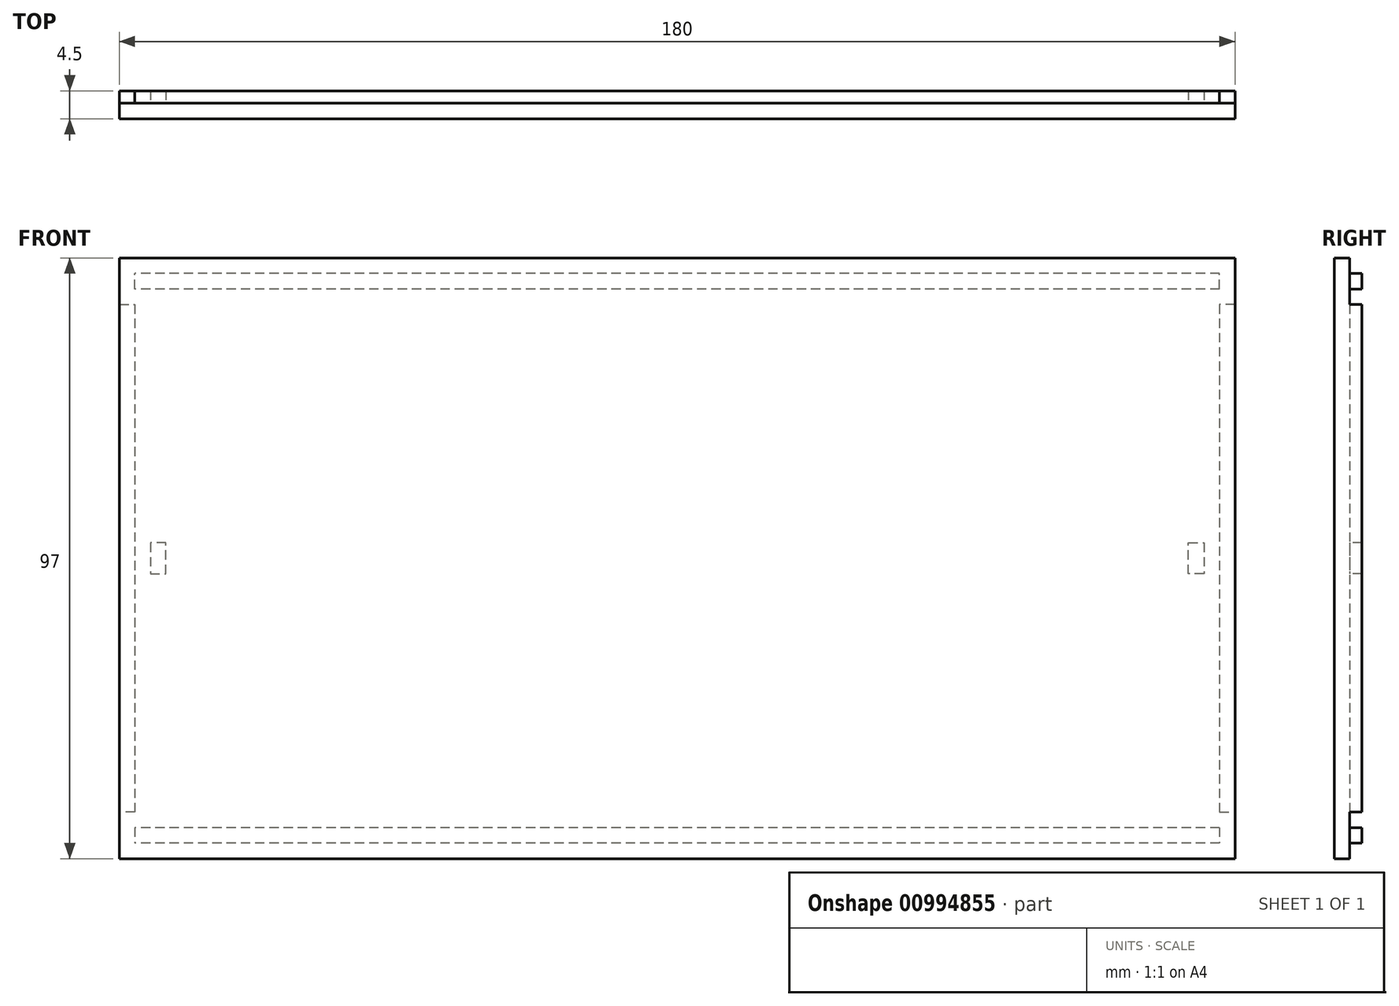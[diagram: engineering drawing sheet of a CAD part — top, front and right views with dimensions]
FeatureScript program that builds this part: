
annotation { "Feature Type Name" : "Feature", "Feature Type Description" : "" }
export const myFeature = defineFeature(function(context is Context, id is Id, definition is map)
    precondition{}
    {
        {
            var Q0;
            Q0=qCreatedBy(makeId("Front.planeOp"),FACE);
            var sketch = newSketch(context, id + "F0", { "sketchPlane" : qUnion([Q0])});
            skLineSegment(sketch, "E0.bottom", {"start": v(-85.95, 51.9) * mm, "end": v(94.05, 51.9) * mm});
            skLineSegment(sketch, "E0.top", {"start": v(-85.95, -45.1) * mm, "end": v(94.05, -45.1) * mm});
            skLineSegment(sketch, "E0.left", {"start": v(-85.95, 51.9) * mm, "end": v(-85.95, -45.1) * mm});
            skLineSegment(sketch, "E0.right", {"start": v(94.05, 51.9) * mm, "end": v(94.05, -45.1) * mm});
            skSolve(sketch);
        }
        {
            var Q0;
            Q0=makeQuery(id+"F0.imprint","IMPRINT",FACE,{"disambiguationData":[TD([[makeQuery(id+"F0.imprint","IMPRINT",EDGE,{"derivedFrom":sQuery(id+"F0.wireOp",EDGE,"E0.bottom")}),-1.0]])]});
            extrude(context, id + "F1", {"entities" : qUnion([Q0]), "depth" : 2.5 * mm, "offsetDistance" : 25 * mm});
        }
        {
            var Q0;
            Q0=makeQuery(id+"F1.opExtrude","CAP_FACE",FACE,{"disambiguationData":[OSD([sQuery(id+"F0.wireOp",EDGE,"E0.bottom"),sQuery(id+"F0.wireOp",EDGE,"E0.top"),sQuery(id+"F0.wireOp",EDGE,"E0.left"),sQuery(id+"F0.wireOp",EDGE,"E0.right")])],"isStart":true});
            var sketch = newSketch(context, id + "F2", { "sketchPlane" : qUnion([Q0])});
            skLineSegment(sketch, "E1.bottom", {"start": v(-91.55, -40.1) * mm, "end": v(83.45, -40.1) * mm});
            skLineSegment(sketch, "E1.top", {"start": v(-91.55, -42.6) * mm, "end": v(83.45, -42.6) * mm});
            skLineSegment(sketch, "E1.left", {"start": v(-91.55, -40.1) * mm, "end": v(-91.55, -42.6) * mm});
            skLineSegment(sketch, "E1.right", {"start": v(83.45, -40.1) * mm, "end": v(83.45, -42.6) * mm});
            skLineSegment(sketch, "E2", {"start": v(-94.05, 3.4) * mm, "end": v(85.95, 3.4) * mm, "construction": true});
            skLineSegment(sketch, "E3.MirrorCS", {"start": v(-91.55, 46.9) * mm, "end": v(-91.55, 49.4) * mm});
            skLineSegment(sketch, "E4.MirrorCS", {"start": v(83.45, 46.9) * mm, "end": v(83.45, 49.4) * mm});
            skLineSegment(sketch, "E5.MirrorCS", {"start": v(-91.55, 46.9) * mm, "end": v(83.45, 46.9) * mm});
            skLineSegment(sketch, "E6.MirrorCS", {"start": v(-91.55, 49.4) * mm, "end": v(83.45, 49.4) * mm});
            skLineSegment(sketch, "E7", {"start": v(83.45, 44.4) * mm, "end": v(83.45, -37.6) * mm});
            skLineSegment(sketch, "E8", {"start": v(83.45, -37.6) * mm, "end": v(85.95, -37.6) * mm});
            skLineSegment(sketch, "E9", {"start": v(85.95, -37.6) * mm, "end": v(85.95, 44.4) * mm});
            skLineSegment(sketch, "E10", {"start": v(85.95, 44.4) * mm, "end": v(83.45, 44.4) * mm});
            skLineSegment(sketch, "E11", {"start": v(-4.05, 51.9) * mm, "end": v(-4.05, -45.1) * mm, "construction": true});
            skLineSegment(sketch, "E12.MirrorCS", {"start": v(-91.55, -37.6) * mm, "end": v(-94.05, -37.6) * mm});
            skLineSegment(sketch, "E13.MirrorCS", {"start": v(85.95, 3.4) * mm, "end": v(-94.05, 3.4) * mm, "construction": true});
            skLineSegment(sketch, "E14.MirrorCS", {"start": v(-91.55, 44.4) * mm, "end": v(-91.55, -37.6) * mm});
            skLineSegment(sketch, "E15.MirrorCS", {"start": v(-94.05, -37.6) * mm, "end": v(-94.05, 44.4) * mm});
            skLineSegment(sketch, "E16.MirrorCS", {"start": v(-94.05, 44.4) * mm, "end": v(-91.55, 44.4) * mm});
            skLineSegment(sketch, "E17", {"start": v(80.95, 5.9) * mm, "end": v(80.95, 0.9) * mm});
            skLineSegment(sketch, "E18", {"start": v(80.95, 0.9) * mm, "end": v(78.45, 0.9) * mm});
            skLineSegment(sketch, "E19", {"start": v(78.45, 0.9) * mm, "end": v(78.45, 5.9) * mm});
            skLineSegment(sketch, "E20", {"start": v(78.45, 5.9) * mm, "end": v(80.95, 5.9) * mm});
            skLineSegment(sketch, "E21.MirrorCS", {"start": v(-89.05, 5.9) * mm, "end": v(-89.05, 0.9) * mm});
            skLineSegment(sketch, "E22.MirrorCS", {"start": v(-86.55, 0.9) * mm, "end": v(-86.55, 5.9) * mm});
            skLineSegment(sketch, "E23.MirrorCS", {"start": v(-86.55, 5.9) * mm, "end": v(-89.05, 5.9) * mm});
            skLineSegment(sketch, "E24.MirrorCS", {"start": v(-89.05, 0.9) * mm, "end": v(-86.55, 0.9) * mm});
            skSolve(sketch);
        }
        {
            var Q0;
            Q0 = qSketchRegion(id + "F2", true);
            extrude(context, id + "F3", {"entities" : qUnion([Q0]), "operationType" : NewBodyOperationType.ADD, "depth" : 2 * mm, "offsetDistance" : 25 * mm});
        }
    });
